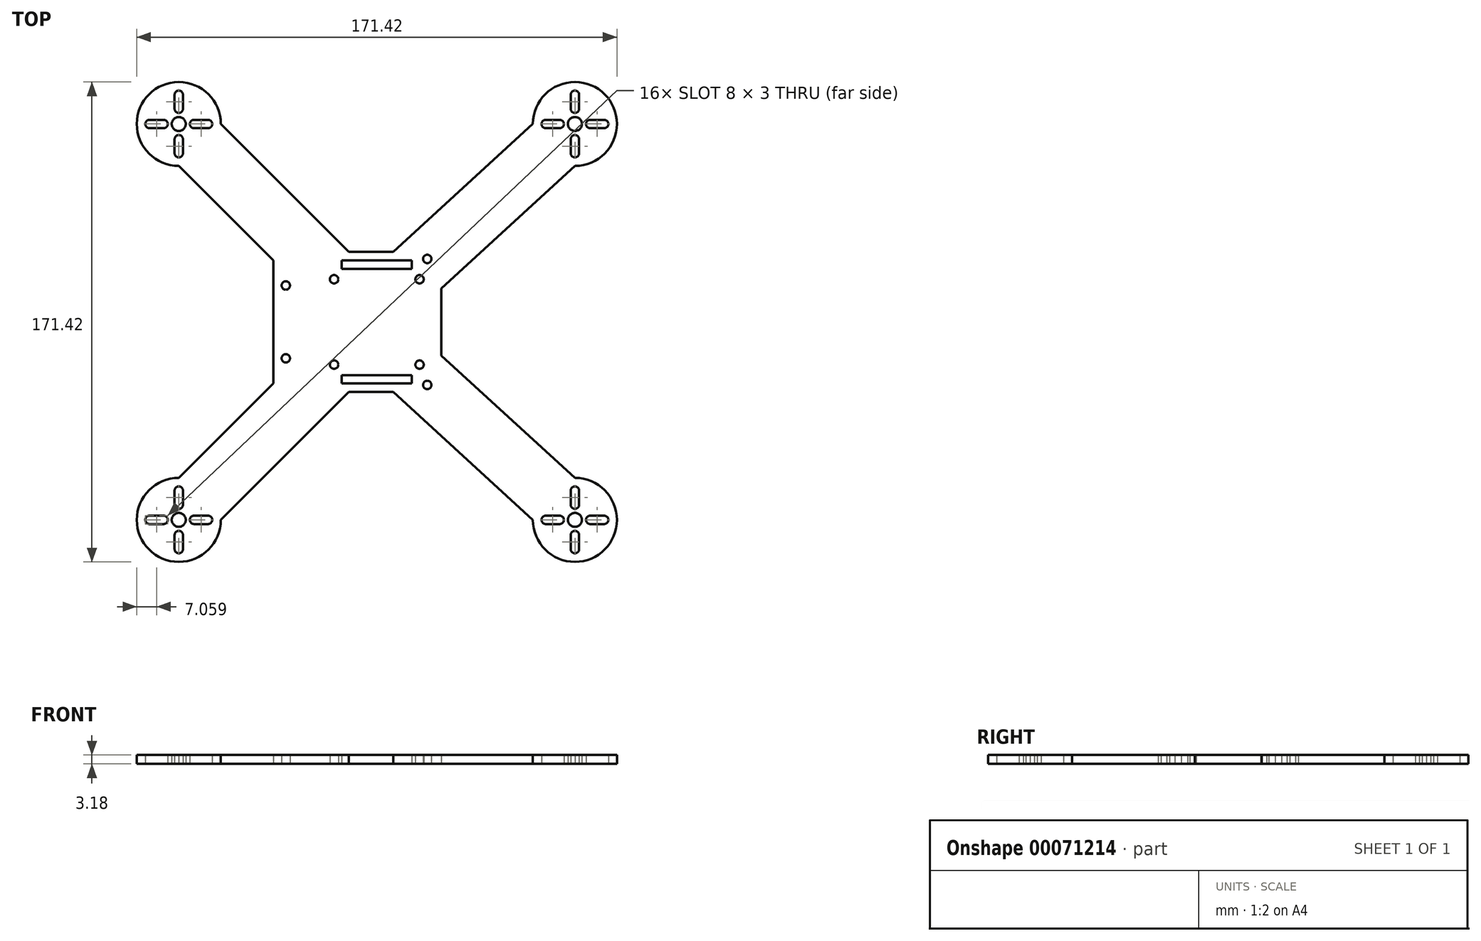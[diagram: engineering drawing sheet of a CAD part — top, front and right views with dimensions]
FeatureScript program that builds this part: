
annotation { "Feature Type Name" : "Feature", "Feature Type Description" : "" }
export const myFeature = defineFeature(function(context is Context, id is Id, definition is map)
    precondition{}
    {
        {
            var Q0;
            Q0=qCreatedBy(makeId("Top.planeOp"),FACE);
            var sketch = newSketch(context, id + "F0", { "sketchPlane" : qUnion([Q0])});
            skLineSegment(sketch, "E0.rect.bottom", {"start": v(70.71, -70.71) * mm, "end": v(-70.71, -70.71) * mm, "construction": true});
            skLineSegment(sketch, "E0.rect.left", {"start": v(70.71, -70.71) * mm, "end": v(70.71, 70.71) * mm, "construction": true});
            skLineSegment(sketch, "E0.rect.right", {"start": v(-70.71, -70.71) * mm, "end": v(-70.71, 70.71) * mm, "construction": true});
            skPoint(sketch, "E0.rect.middle", {"position": v(0, 0) * mm});
            skArc(sketch, "E1", {"start": v(-55.71, 70.71) * mm, "mid": v(-81.32, 81.32) * mm, "end": v(-70.71, 55.71) * mm});
            skLineSegment(sketch, "E2", {"start": v(70.71, 70.71) * mm, "end": v(-70.71, -70.71) * mm, "construction": true});
            skLineSegment(sketch, "E3", {"start": v(70.71, -70.71) * mm, "end": v(-70.71, 70.71) * mm, "construction": true});
            skCircle(sketch, "E4", {"center": v(-70.71, 70.71) * mm, "radius": 2.5 * mm});
            skLineSegment(sketch, "E5.rect.left", {"start": v(-69.21, 76.15) * mm, "end": v(-69.21, 81.15) * mm});
            skLineSegment(sketch, "E5.rect.right", {"start": v(-72.21, 76.15) * mm, "end": v(-72.21, 81.15) * mm});
            skArc(sketch, "E6", {"start": v(-69.21, 81.15) * mm, "mid": v(-70.71, 82.65) * mm, "end": v(-72.21, 81.15) * mm});
            skArc(sketch, "E7", {"start": v(-72.21, 76.15) * mm, "mid": v(-70.71, 74.65) * mm, "end": v(-69.21, 76.15) * mm});
            skLineSegment(sketch, "E8", {"start": v(-70.71, 70.71) * mm, "end": v(70.71, 70.71) * mm, "construction": true});
            skCircle(sketch, "E9.MirrorC", {"center": v(-70.71, -70.71) * mm, "radius": 2.5 * mm});
            skArc(sketch, "E10.MirrorC", {"start": v(-55.71, -70.71) * mm, "mid": v(-81.32, -81.32) * mm, "end": v(-70.71, -55.71) * mm});
            skCircle(sketch, "E11.MirrorC", {"center": v(70.71, -70.71) * mm, "radius": 2.5 * mm});
            skArc(sketch, "E12.MirrorC", {"start": v(55.71, -70.71) * mm, "mid": v(81.32, -81.32) * mm, "end": v(70.71, -55.71) * mm});
            skCircle(sketch, "E13.MirrorC", {"center": v(70.71, 70.71) * mm, "radius": 2.5 * mm});
            skArc(sketch, "E14.MirrorC", {"start": v(55.71, 70.71) * mm, "mid": v(81.32, 81.32) * mm, "end": v(70.71, 55.71) * mm});
            skLineSegment(sketch, "E15.rect.bottom", {"start": v(18, 18) * mm, "end": v(-18, 18) * mm, "construction": true});
            skLineSegment(sketch, "E15.rect.top", {"start": v(18, -18) * mm, "end": v(-18, -18) * mm, "construction": true});
            skLineSegment(sketch, "E15.rect.left", {"start": v(18, 18) * mm, "end": v(18, -18) * mm, "construction": true});
            skLineSegment(sketch, "E15.rect.right", {"start": v(-18, 18) * mm, "end": v(-18, -18) * mm, "construction": true});
            skLineSegment(sketch, "E16.rect.top", {"start": v(-10, 25) * mm, "end": v(5.83, 25) * mm});
            skLineSegment(sketch, "E16.rect.left", {"start": v(-37, -22) * mm, "end": v(-37, 22) * mm});
            skCircle(sketch, "E17", {"center": v(18, -22.5) * mm, "radius": 1.5 * mm});
            skCircle(sketch, "E18.MirrorC", {"center": v(18, 22.5) * mm, "radius": 1.5 * mm});
            skLineSegment(sketch, "E19", {"start": v(70.71, -55.71) * mm, "end": v(23, -12) * mm});
            skLineSegment(sketch, "E20", {"start": v(55.71, -70.71) * mm, "end": v(5.83, -25) * mm});
            skLineSegment(sketch, "E21.MirrorCS", {"start": v(70.71, 55.71) * mm, "end": v(23, 12) * mm});
            skLineSegment(sketch, "E22.MirrorCS", {"start": v(55.71, 70.71) * mm, "end": v(5.83, 25) * mm});
            skLineSegment(sketch, "E23", {"start": v(-55.71, -70.71) * mm, "end": v(-10, -25) * mm});
            skLineSegment(sketch, "E24", {"start": v(-70.71, -55.71) * mm, "end": v(-37, -22) * mm});
            skLineSegment(sketch, "E25.MirrorCS", {"start": v(-70.71, 55.71) * mm, "end": v(-37, 22) * mm});
            skLineSegment(sketch, "E26.MirrorCS", {"start": v(-55.71, 70.71) * mm, "end": v(-10, 25) * mm});
            skCircle(sketch, "E27", {"center": v(-32.5, -13) * mm, "radius": 1.5 * mm});
            skCircle(sketch, "E28.MirrorC", {"center": v(-32.5, 13) * mm, "radius": 1.5 * mm});
            skLineSegment(sketch, "E29.trimOffspring", {"start": v(23, 12) * mm, "end": v(23, -12) * mm});
            skLineSegment(sketch, "E30.trimOffspring", {"start": v(-10, -25) * mm, "end": v(5.83, -25) * mm});
            skLineSegment(sketch, "E31", {"start": v(-70.71, 70.71) * mm, "end": v(-68.94, 72.48) * mm});
            skLineSegment(sketch, "E32", {"start": v(-70.71, 70.71) * mm, "end": v(-72.48, 68.94) * mm});
            skLineSegment(sketch, "E33.MirrorCS", {"start": v(-69.21, 65.27) * mm, "end": v(-69.21, 60.27) * mm});
            skArc(sketch, "E34.MirrorCS", {"start": v(-69.21, 60.27) * mm, "mid": v(-70.71, 58.77) * mm, "end": v(-72.21, 60.27) * mm});
            skLineSegment(sketch, "E35.MirrorCS", {"start": v(-72.21, 65.27) * mm, "end": v(-72.21, 60.27) * mm});
            skArc(sketch, "E36.MirrorCS", {"start": v(-72.21, 65.27) * mm, "mid": v(-70.71, 66.77) * mm, "end": v(-69.21, 65.27) * mm});
            skLineSegment(sketch, "E37.MirrorCS", {"start": v(-65.27, 69.21) * mm, "end": v(-60.27, 69.21) * mm});
            skArc(sketch, "E38.MirrorCS", {"start": v(-65.27, 72.21) * mm, "mid": v(-66.77, 70.71) * mm, "end": v(-65.27, 69.21) * mm});
            skLineSegment(sketch, "E39.MirrorCS", {"start": v(-65.27, 72.21) * mm, "end": v(-60.27, 72.21) * mm});
            skArc(sketch, "E40.MirrorCS", {"start": v(-60.27, 69.21) * mm, "mid": v(-58.77, 70.71) * mm, "end": v(-60.27, 72.21) * mm});
            skLineSegment(sketch, "E41.MirrorCS", {"start": v(-76.15, 69.21) * mm, "end": v(-81.15, 69.21) * mm});
            skArc(sketch, "E42.MirrorCS", {"start": v(-76.15, 69.21) * mm, "mid": v(-74.65, 70.71) * mm, "end": v(-76.15, 72.21) * mm});
            skLineSegment(sketch, "E43.MirrorCS", {"start": v(-76.15, 72.21) * mm, "end": v(-81.15, 72.21) * mm});
            skArc(sketch, "E44.MirrorCS", {"start": v(-81.15, 72.21) * mm, "mid": v(-82.65, 70.71) * mm, "end": v(-81.15, 69.21) * mm});
            skLineSegment(sketch, "E45.MirrorCS", {"start": v(-69.21, -65.27) * mm, "end": v(-69.21, -60.27) * mm});
            skLineSegment(sketch, "E46.MirrorCS", {"start": v(-72.21, -65.27) * mm, "end": v(-72.21, -60.27) * mm});
            skLineSegment(sketch, "E47.MirrorCS", {"start": v(-72.21, -76.15) * mm, "end": v(-72.21, -81.15) * mm});
            skArc(sketch, "E48.MirrorCS", {"start": v(-69.21, -81.15) * mm, "mid": v(-70.71, -82.65) * mm, "end": v(-72.21, -81.15) * mm});
            skLineSegment(sketch, "E49.MirrorCS", {"start": v(-69.21, -76.15) * mm, "end": v(-69.21, -81.15) * mm});
            skArc(sketch, "E50.MirrorCS", {"start": v(-72.21, -76.15) * mm, "mid": v(-70.71, -74.65) * mm, "end": v(-69.21, -76.15) * mm});
            skLineSegment(sketch, "E51.MirrorCS", {"start": v(-65.27, -72.21) * mm, "end": v(-60.27, -72.21) * mm});
            skArc(sketch, "E52.MirrorCS", {"start": v(-60.27, -69.21) * mm, "mid": v(-58.77, -70.71) * mm, "end": v(-60.27, -72.21) * mm});
            skLineSegment(sketch, "E53.MirrorCS", {"start": v(-65.27, -69.21) * mm, "end": v(-60.27, -69.21) * mm});
            skArc(sketch, "E54.MirrorCS", {"start": v(-65.27, -72.21) * mm, "mid": v(-66.77, -70.71) * mm, "end": v(-65.27, -69.21) * mm});
            skArc(sketch, "E55.MirrorCS", {"start": v(-76.15, -69.21) * mm, "mid": v(-74.65, -70.71) * mm, "end": v(-76.15, -72.21) * mm});
            skLineSegment(sketch, "E56.MirrorCS", {"start": v(-76.15, -72.21) * mm, "end": v(-81.15, -72.21) * mm});
            skArc(sketch, "E57.MirrorCS", {"start": v(-81.15, -72.21) * mm, "mid": v(-82.65, -70.71) * mm, "end": v(-81.15, -69.21) * mm});
            skLineSegment(sketch, "E58.MirrorCS", {"start": v(-76.15, -69.21) * mm, "end": v(-81.15, -69.21) * mm});
            skArc(sketch, "E59.MirrorCS", {"start": v(-72.21, -65.27) * mm, "mid": v(-70.71, -66.77) * mm, "end": v(-69.21, -65.27) * mm});
            skArc(sketch, "E60.MirrorCS", {"start": v(-69.21, -60.27) * mm, "mid": v(-70.71, -58.77) * mm, "end": v(-72.21, -60.27) * mm});
            skArc(sketch, "E61.MirrorCS", {"start": v(72.21, 76.15) * mm, "mid": v(70.71, 74.65) * mm, "end": v(69.21, 76.15) * mm});
            skArc(sketch, "E62.MirrorCS", {"start": v(69.21, 81.15) * mm, "mid": v(70.71, 82.65) * mm, "end": v(72.21, 81.15) * mm});
            skLineSegment(sketch, "E63.MirrorCS", {"start": v(69.21, 76.15) * mm, "end": v(69.21, 81.15) * mm});
            skLineSegment(sketch, "E64.MirrorCS", {"start": v(72.21, 76.15) * mm, "end": v(72.21, 81.15) * mm});
            skLineSegment(sketch, "E65.MirrorCS", {"start": v(65.27, 69.21) * mm, "end": v(60.27, 69.21) * mm});
            skArc(sketch, "E66.MirrorCS", {"start": v(76.15, 69.21) * mm, "mid": v(74.65, 70.71) * mm, "end": v(76.15, 72.21) * mm});
            skArc(sketch, "E67.MirrorCS", {"start": v(81.15, 72.21) * mm, "mid": v(82.65, 70.71) * mm, "end": v(81.15, 69.21) * mm});
            skArc(sketch, "E68.MirrorCS", {"start": v(60.27, 69.21) * mm, "mid": v(58.77, 70.71) * mm, "end": v(60.27, 72.21) * mm});
            skArc(sketch, "E69.MirrorCS", {"start": v(65.27, 72.21) * mm, "mid": v(66.77, 70.71) * mm, "end": v(65.27, 69.21) * mm});
            skLineSegment(sketch, "E70.MirrorCS", {"start": v(76.15, 72.21) * mm, "end": v(81.15, 72.21) * mm});
            skLineSegment(sketch, "E71.MirrorCS", {"start": v(65.27, 72.21) * mm, "end": v(60.27, 72.21) * mm});
            skLineSegment(sketch, "E72.MirrorCS", {"start": v(76.15, 69.21) * mm, "end": v(81.15, 69.21) * mm});
            skLineSegment(sketch, "E73.MirrorCS", {"start": v(69.21, 65.27) * mm, "end": v(69.21, 60.27) * mm});
            skArc(sketch, "E74.MirrorCS", {"start": v(69.21, 60.27) * mm, "mid": v(70.71, 58.77) * mm, "end": v(72.21, 60.27) * mm});
            skArc(sketch, "E75.MirrorCS", {"start": v(72.21, 65.27) * mm, "mid": v(70.71, 66.77) * mm, "end": v(69.21, 65.27) * mm});
            skLineSegment(sketch, "E76.MirrorCS", {"start": v(72.21, 65.27) * mm, "end": v(72.21, 60.27) * mm});
            skLineSegment(sketch, "E77.MirrorCS", {"start": v(69.21, -65.27) * mm, "end": v(69.21, -60.27) * mm});
            skLineSegment(sketch, "E78.MirrorCS", {"start": v(72.21, -65.27) * mm, "end": v(72.21, -60.27) * mm});
            skLineSegment(sketch, "E79.MirrorCS", {"start": v(76.15, -69.21) * mm, "end": v(81.15, -69.21) * mm});
            skLineSegment(sketch, "E80.MirrorCS", {"start": v(72.21, -76.15) * mm, "end": v(72.21, -81.15) * mm});
            skArc(sketch, "E81.MirrorCS", {"start": v(72.21, -65.27) * mm, "mid": v(70.71, -66.77) * mm, "end": v(69.21, -65.27) * mm});
            skLineSegment(sketch, "E82.MirrorCS", {"start": v(65.27, -69.21) * mm, "end": v(60.27, -69.21) * mm});
            skLineSegment(sketch, "E83.MirrorCS", {"start": v(69.21, -76.15) * mm, "end": v(69.21, -81.15) * mm});
            skLineSegment(sketch, "E84.MirrorCS", {"start": v(76.15, -72.21) * mm, "end": v(81.15, -72.21) * mm});
            skArc(sketch, "E85.MirrorCS", {"start": v(60.27, -69.21) * mm, "mid": v(58.77, -70.71) * mm, "end": v(60.27, -72.21) * mm});
            skArc(sketch, "E86.MirrorCS", {"start": v(65.27, -72.21) * mm, "mid": v(66.77, -70.71) * mm, "end": v(65.27, -69.21) * mm});
            skArc(sketch, "E87.MirrorCS", {"start": v(72.21, -76.15) * mm, "mid": v(70.71, -74.65) * mm, "end": v(69.21, -76.15) * mm});
            skArc(sketch, "E88.MirrorCS", {"start": v(76.15, -69.21) * mm, "mid": v(74.65, -70.71) * mm, "end": v(76.15, -72.21) * mm});
            skArc(sketch, "E89.MirrorCS", {"start": v(69.21, -60.27) * mm, "mid": v(70.71, -58.77) * mm, "end": v(72.21, -60.27) * mm});
            skLineSegment(sketch, "E90.MirrorCS", {"start": v(65.27, -72.21) * mm, "end": v(60.27, -72.21) * mm});
            skArc(sketch, "E91.MirrorCS", {"start": v(81.15, -72.21) * mm, "mid": v(82.65, -70.71) * mm, "end": v(81.15, -69.21) * mm});
            skArc(sketch, "E92.MirrorCS", {"start": v(69.21, -81.15) * mm, "mid": v(70.71, -82.65) * mm, "end": v(72.21, -81.15) * mm});
            skCircle(sketch, "E93", {"center": v(-15.25, 15.25) * mm, "radius": 1.5 * mm});
            skCircle(sketch, "E94.MirrorC", {"center": v(15.25, 15.25) * mm, "radius": 1.5 * mm});
            skCircle(sketch, "E95.MirrorC", {"center": v(-15.25, -15.25) * mm, "radius": 1.5 * mm});
            skCircle(sketch, "E96.MirrorC", {"center": v(15.25, -15.25) * mm, "radius": 1.5 * mm});
            skLineSegment(sketch, "E97.rect.bottom", {"start": v(-12.5, 22) * mm, "end": v(12.5, 22) * mm});
            skLineSegment(sketch, "E97.rect.top", {"start": v(-12.5, 19) * mm, "end": v(12.5, 19) * mm});
            skLineSegment(sketch, "E97.rect.left", {"start": v(-12.5, 22) * mm, "end": v(-12.5, 19) * mm});
            skLineSegment(sketch, "E97.rect.right", {"start": v(12.5, 22) * mm, "end": v(12.5, 19) * mm});
            skPoint(sketch, "E97.rect.middle", {"position": v(0, 20.5) * mm});
            skPoint(sketch, "E98.MirrorP", {"position": v(0, -20.5) * mm});
            skLineSegment(sketch, "E99.MirrorCS", {"start": v(-12.5, -19) * mm, "end": v(12.5, -19) * mm});
            skLineSegment(sketch, "E100.MirrorCS", {"start": v(-12.5, -22) * mm, "end": v(-12.5, -19) * mm});
            skLineSegment(sketch, "E101.MirrorCS", {"start": v(-12.5, -22) * mm, "end": v(12.5, -22) * mm});
            skLineSegment(sketch, "E102.MirrorCS", {"start": v(12.5, -22) * mm, "end": v(12.5, -19) * mm});
            skSolve(sketch);
        }
        {
            var Q0;
            Q0=makeQuery(id+"F0.imprint","IMPRINT",FACE,{"disambiguationData":[TD([[makeQuery(id+"F0.imprint","IMPRINT",EDGE,{"derivedFrom":sQuery(id+"F0.wireOp",EDGE,"E1")}),1.0]])]});
            extrude(context, id + "F1", {"entities" : qUnion([Q0]), "depth" : 3.17 * mm});
        }
    });
